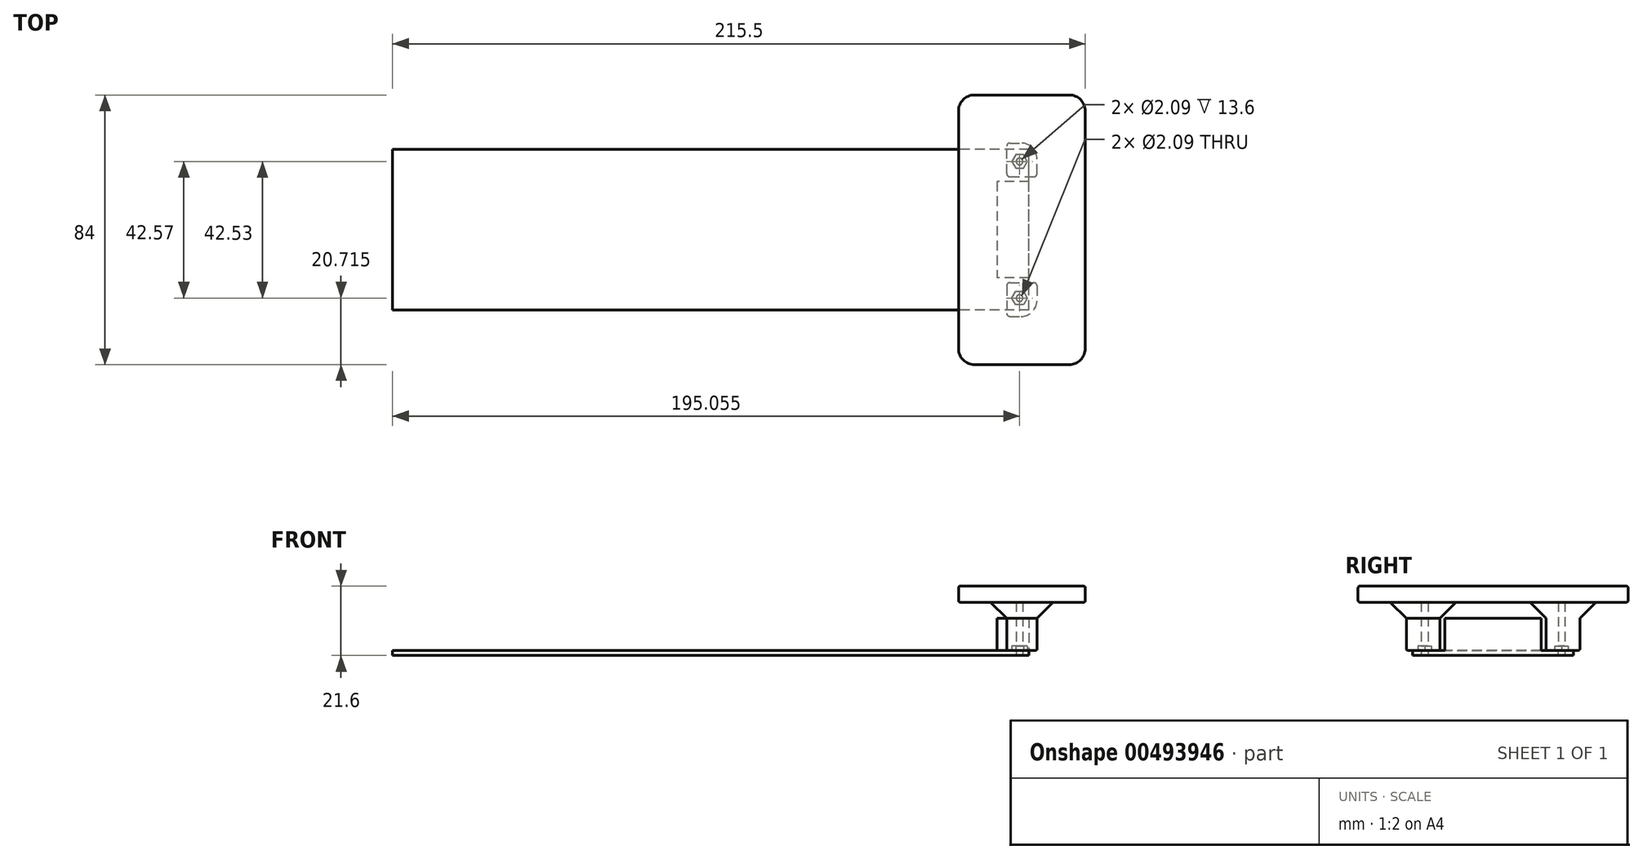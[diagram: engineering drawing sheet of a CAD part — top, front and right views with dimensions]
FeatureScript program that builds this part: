
annotation { "Feature Type Name" : "Feature", "Feature Type Description" : "" }
export const myFeature = defineFeature(function(context is Context, id is Id, definition is map)
    precondition{}
    {
        {
            var Q0;
            Q0=qCreatedBy(makeId("Top.planeOp"),FACE);
            var sketch = newSketch(context, id + "F0", { "sketchPlane" : qUnion([Q0])});
            skLineSegment(sketch, "E0.bottom", {"start": v(0, 0) * mm, "end": v(-198, 0) * mm});
            skLineSegment(sketch, "E0.top", {"start": v(0, 50) * mm, "end": v(-198, 50) * mm});
            skLineSegment(sketch, "E0.left", {"start": v(0, 0) * mm, "end": v(0, 50) * mm});
            skLineSegment(sketch, "E0.right", {"start": v(-198, 0) * mm, "end": v(-198, 50) * mm});
            skCircle(sketch, "E1", {"center": v(-2.95, 3.71) * mm, "radius": 1.04 * mm});
            skCircle(sketch, "E2", {"center": v(-2.95, 46.25) * mm, "radius": 1.04 * mm});
            skLineSegment(sketch, "E3", {"start": v(-2.95, 47.3) * mm, "end": v(-2.95, 50) * mm, "construction": true});
            skLineSegment(sketch, "E4", {"start": v(-1.9, 46.25) * mm, "end": v(0, 46.25) * mm, "construction": true});
            skLineSegment(sketch, "E5", {"start": v(0, 3.71) * mm, "end": v(-1.9, 3.71) * mm, "construction": true});
            skLineSegment(sketch, "E6", {"start": v(-2.95, 2.67) * mm, "end": v(-2.94, 0) * mm, "construction": true});
            skSolve(sketch);
        }
        {
            var Q0;
            Q0 = qSketchRegion(id + "F0", true);
            extrude(context, id + "F1", {"entities" : qUnion([Q0]), "depth" : 1.6 * mm});
        }
        {
            var Q0;
            Q0=makeQuery(id+"F1.opExtrude","CAP_FACE",FACE,{"disambiguationData":[OSD([sQuery(id+"F0.wireOp",EDGE,"E0.bottom"),sQuery(id+"F0.wireOp",EDGE,"E0.top"),sQuery(id+"F0.wireOp",EDGE,"E0.left"),sQuery(id+"F0.wireOp",EDGE,"E0.right"),sQuery(id+"F0.wireOp",EDGE,"E1"),sQuery(id+"F0.wireOp",EDGE,"E2")])],"isStart":false});
            var sketch = newSketch(context, id + "F2", { "sketchPlane" : qUnion([Q0])});
            skLineSegment(sketch, "E7.bottom", {"start": v(0, 40) * mm, "end": v(-10, 40) * mm});
            skLineSegment(sketch, "E7.top", {"start": v(0, 10) * mm, "end": v(-10, 10) * mm});
            skLineSegment(sketch, "E7.left", {"start": v(0, 40) * mm, "end": v(0, 10) * mm});
            skLineSegment(sketch, "E7.right", {"start": v(-10, 40) * mm, "end": v(-10, 10) * mm});
            skLineSegment(sketch, "E8", {"start": v(-10, 40) * mm, "end": v(-10, 50) * mm, "construction": true});
            skLineSegment(sketch, "E9", {"start": v(-10, 10) * mm, "end": v(-10, 0) * mm, "construction": true});
            skSolve(sketch);
        }
        {
            var Q0;
            Q0=makeQuery(id+"F2.imprint","IMPRINT",FACE,{"disambiguationData":[TD([[makeQuery(id+"F2.imprint","IMPRINT",EDGE,{"derivedFrom":sQuery(id+"F2.wireOp",EDGE,"E7.bottom")}),1.0]])]});
            extrude(context, id + "F3", {"entities" : qUnion([Q0]), "operationType" : NewBodyOperationType.ADD, "depth" : 10 * mm});
        }
        {
            var Q0;
            Q0=makeQuery(id+"F1.opExtrude","CAP_FACE",FACE,{"disambiguationData":[OSD([sQuery(id+"F0.wireOp",EDGE,"E0.bottom"),sQuery(id+"F0.wireOp",EDGE,"E0.top"),sQuery(id+"F0.wireOp",EDGE,"E0.left"),sQuery(id+"F0.wireOp",EDGE,"E0.right"),sQuery(id+"F0.wireOp",EDGE,"E1"),sQuery(id+"F0.wireOp",EDGE,"E2")])],"isStart":false});
            var sketch = newSketch(context, id + "F4", { "sketchPlane" : qUnion([Q0])});
            skCircle(sketch, "E10", {"center": v(-2.95, 3.71) * mm, "radius": 0.85 * mm});
            skLineSegment(sketch, "E11.bottom", {"start": v(-6.95, 8.5) * mm, "end": v(2.5, 8.5) * mm});
            skLineSegment(sketch, "E11.top", {"start": v(-6.94, -2) * mm, "end": v(2.5, -2) * mm});
            skLineSegment(sketch, "E11.left", {"start": v(-6.95, 8.5) * mm, "end": v(-6.95, -2) * mm});
            skLineSegment(sketch, "E11.right", {"start": v(2.5, 8.5) * mm, "end": v(2.5, -2) * mm});
            skLineSegment(sketch, "E12", {"start": v(-6.95, 3.71) * mm, "end": v(2.5, 3.71) * mm, "construction": true});
            skLineSegment(sketch, "E13", {"start": v(-2.95, -2) * mm, "end": v(-2.95, 8.5) * mm, "construction": true});
            skLineSegment(sketch, "E14.0", {"start": v(0, 0) * mm, "end": v(-198, 0) * mm, "construction": true});
            skLineSegment(sketch, "E14.1", {"start": v(0, 0) * mm, "end": v(0, 10) * mm, "construction": true});
            skSolve(sketch);
        }
        {
            var Q0;
            {var subQ2=sQuery(id+"F4.wireOp",EDGE,"E11.top");Q0=makeQuery(id+"F4.imprint","IMPRINT",FACE,{"disambiguationData":[TD([[makeQuery(id+"F4.imprint","IMPRINT",EDGE,{"derivedFrom":subQ2}),1.0]])]});}
            var Q1;
            {var subQ0=sQuery(id+"F0.wireOp",EDGE,"E1");Q1=makeQuery(id+"F4.imprint","IMPRINT",FACE,{"disambiguationData":[TD([[makeQuery(id+"F4.imprint","IMPRINT",EDGE,{"derivedFrom":makeQuery(id+"F1.opExtrude","CAP_EDGE",EDGE,{"disambiguationData":[OSD([subQ0])],"isStart":false})}),-1.0]])]});}
            extrude(context, id + "F5", {"entities" : qUnion([Q0, Q1]), "depth" : 15 * mm});
        }
        {
            var Q0;
            Q0=makeQuery(id+"F5.opExtrude","SWEPT_EDGE",EDGE,{"disambiguationData":[OSD([sQuery(id+"F4.wireOp",EDGE,"E11.top"),sQuery(id+"F4.wireOp",EDGE,"E11.right")])]});
            fillet(context, id + "F6", {"entities" : qUnion([Q0]), "radius" : 5 * mm, "tangentPropagation" : true, "allowEdgeOverflow" : false});
        }
        {
            var Q0;
            Q0=makeQuery(id+"F5.opExtrude","CAP_FACE",FACE,{"disambiguationData":[OSD([sQuery(id+"F0.wireOp",EDGE,"E1"),sQuery(id+"F4.wireOp",EDGE,"E11.bottom"),sQuery(id+"F4.wireOp",EDGE,"E11.top"),sQuery(id+"F4.wireOp",EDGE,"E11.left"),sQuery(id+"F4.wireOp",EDGE,"E11.right")])],"isStart":true});
            var sketch = newSketch(context, id + "F7", { "sketchPlane" : qUnion([Q0])});
            skCircle(sketch, "E15", {"center": v(-2.95, -3.71) * mm, "radius": 2.1 * mm, "construction": true});
            skLineSegment(sketch, "E16", {"start": v(-1.73, -1.61) * mm, "end": v(-4.16, -1.61) * mm});
            skLineSegment(sketch, "E17", {"start": v(-4.16, -1.61) * mm, "end": v(-5.37, -3.71) * mm});
            skLineSegment(sketch, "E18", {"start": v(-5.37, -3.71) * mm, "end": v(-4.16, -5.81) * mm});
            skLineSegment(sketch, "E19", {"start": v(-4.16, -5.81) * mm, "end": v(-1.73, -5.81) * mm});
            skLineSegment(sketch, "E20", {"start": v(-1.73, -5.81) * mm, "end": v(-0.52, -3.72) * mm});
            skLineSegment(sketch, "E21", {"start": v(-0.52, -3.71) * mm, "end": v(-1.73, -1.61) * mm});
            skSolve(sketch);
        }
        {
            var Q0;
            Q0 = qSketchRegion(id + "F7", true);
            extrude(context, id + "F8", {"entities" : qUnion([Q0]), "operationType" : NewBodyOperationType.REMOVE, "oppositeDirection" : true, "depth" : 1.4 * mm, "offsetDistance" : 25 * mm});
        }
        {
            var Q0;
            Q0=makeQuery(id+"F5.opExtrude","SWEPT_EDGE",EDGE,{"disambiguationData":[OSD([sQuery(id+"F4.wireOp",EDGE,"E11.top"),sQuery(id+"F4.wireOp",EDGE,"E11.left")])]});
            var Q1;
            Q1=makeQuery(id+"F5.opExtrude","SWEPT_EDGE",EDGE,{"disambiguationData":[OSD([sQuery(id+"F4.wireOp",EDGE,"E11.bottom"),sQuery(id+"F4.wireOp",EDGE,"E11.right")])]});
            var Q2;
            Q2=makeQuery(id+"F5.opExtrude","SWEPT_EDGE",EDGE,{"disambiguationData":[OSD([sQuery(id+"F4.wireOp",EDGE,"E11.bottom"),sQuery(id+"F4.wireOp",EDGE,"E11.left")])]});
            fillet(context, id + "F9", {"entities" : qUnion([Q0, Q1, Q2]), "radius" : 1 * mm, "tangentPropagation" : true, "allowEdgeOverflow" : false});
        }
        {
            var Q0;
            Q0=makeQuery(id+"F1.opExtrude","CAP_EDGE",EDGE,{"disambiguationData":[OSD([sQuery(id+"F0.wireOp",EDGE,"E0.left")])],"isStart":true});
            cPoint(context, id + "F10", {"entities" : qUnion([Q0]), "parameter" : 0.5});
        }
        {
            var Q0;
            Q0=makeQuery(id+"F3.opExtrude","CAP_EDGE",EDGE,{"disambiguationData":[OSD([sQuery(id+"F2.wireOp",EDGE,"E7.left")])],"isStart":false});
            cPoint(context, id + "F11", {"entities" : qUnion([Q0]), "parameter" : 0.5});
        }
        {
            var Q0;
            Q0=makeQuery(id+"F3.opExtrude","CAP_EDGE",EDGE,{"disambiguationData":[OSD([sQuery(id+"F2.wireOp",EDGE,"E7.right")])],"isStart":false});
            cPoint(context, id + "F12", {"entities" : qUnion([Q0]), "parameter" : 0.5});
        }
        {
            var Q0;
            Q0 = qCreatedBy(id + "F10" ,VERTEX);
            var Q1;
            Q1 = qCreatedBy(id + "F11" ,VERTEX);
            var Q2;
            Q2 = qCreatedBy(id + "F12" ,VERTEX);
            cPlane(context, id + "F13", {"entities" : qUnion([Q0, Q1, Q2]), "cplaneType" : CPlaneType.THREE_POINT, "offset" : 25 * mm, "width" : 150 * mm, "height" : 150 * mm});
        }
        {
            var Q0;
            Q0=makeQuery(id+"F5.opExtrude","SWEPT_BODY",BODY,{"disambiguationData":[OSD([sQuery(id+"F0.wireOp",EDGE,"E1"),sQuery(id+"F4.wireOp",EDGE,"E11.bottom"),sQuery(id+"F4.wireOp",EDGE,"E11.top"),sQuery(id+"F4.wireOp",EDGE,"E11.left"),sQuery(id+"F4.wireOp",EDGE,"E11.right")])]});
            var Q1;
            Q1=qCreatedBy(id+"F13.planeOp",FACE);
            mirror(context, id + "F14", {"entities" : qUnion([Q0]), "mirrorPlane" : qUnion([Q1])});
        }
        {
            var Q0;
            Q0=makeQuery(id+"F5.opExtrude","CAP_FACE",FACE,{"disambiguationData":[OSD([sQuery(id+"F0.wireOp",EDGE,"E1"),sQuery(id+"F4.wireOp",EDGE,"E11.bottom"),sQuery(id+"F4.wireOp",EDGE,"E11.top"),sQuery(id+"F4.wireOp",EDGE,"E11.left"),sQuery(id+"F4.wireOp",EDGE,"E11.right")])],"isStart":false});
            var sketch = newSketch(context, id + "F15", { "sketchPlane" : qUnion([Q0])});
            skLineSegment(sketch, "E22.bottom", {"start": v(-21.94, -17) * mm, "end": v(17.5, -17) * mm});
            skLineSegment(sketch, "E22.top", {"start": v(-21.95, 67) * mm, "end": v(17.5, 67) * mm});
            skLineSegment(sketch, "E22.left", {"start": v(-21.94, -17) * mm, "end": v(-21.95, 67) * mm});
            skLineSegment(sketch, "E22.right", {"start": v(17.5, -17) * mm, "end": v(17.5, 67) * mm});
            skLineSegment(sketch, "E23.2", {"start": v(17.5, 67) * mm, "end": v(17.5, -17) * mm});
            skPoint(sketch, "E24", {"position": v(17.5, 67) * mm});
            skPoint(sketch, "E25.0", {"position": v(0, 25) * mm});
            skPoint(sketch, "E26", {"position": v(17.5, 25) * mm});
            skSolve(sketch);
        }
        {
            var Q0;
            Q0=makeQuery(id+"F15.imprint","IMPRINT",FACE,{"disambiguationData":[TD([[makeQuery(id+"F15.imprint","IMPRINT",EDGE,{"derivedFrom":sQuery(id+"F15.wireOp",EDGE,"E22.top")}),-1.0]])]});
            var Q1;
            {var subQ4=sQuery(id+"F0.wireOp",EDGE,"E1");Q1=makeQuery(id+"F15.imprint","IMPRINT",FACE,{"disambiguationData":[TD([[makeQuery(id+"F15.imprint","IMPRINT",EDGE,{"derivedFrom":makeQuery(id+"F5.opExtrude","CAP_EDGE",EDGE,{"disambiguationData":[OSD([subQ4])],"isStart":false})}),-1.0]])]});}
            var Q2;
            Q2=makeQuery(id+"F15.imprint","IMPRINT",FACE,{"disambiguationData":[TD([[makeQuery(id+"F15.imprint","IMPRINT",EDGE,{"derivedFrom":makeQuery(id+"F5.opExtrude","CAP_EDGE",EDGE,{"disambiguationData":[OSD([sQuery(id+"F0.wireOp",EDGE,"E1")])],"isStart":false})}),1.0]])]});
            extrude(context, id + "F16", {"entities" : qUnion([Q0, Q1, Q2]), "operationType" : NewBodyOperationType.ADD, "depth" : 5 * mm});
        }
        {
            var Q0;
            {var subQ0=sQuery(id+"F4.wireOp",EDGE,"E11.right");var subQ1=sQuery(id+"F4.wireOp",EDGE,"E11.top");Q0=makeQuery(id+"F14.opPattern","COPY",EDGE,{"derivedFrom":makeQuery(id+"F6.opFillet","BLEND_EDGE",EDGE,{"blendedFrom":[makeQuery(id+"F5.opExtrude","SWEPT_EDGE",EDGE,{"disambiguationData":[OSD([subQ1,subQ0])]}),makeQuery(id+"F5.opExtrude","CAP_FACE",FACE,{"disambiguationData":[OSD([sQuery(id+"F0.wireOp",EDGE,"E1"),sQuery(id+"F4.wireOp",EDGE,"E11.bottom"),subQ1,sQuery(id+"F4.wireOp",EDGE,"E11.left"),subQ0])],"isStart":false})],"blendedInto":[makeQuery(id+"F5.opExtrude","CAP_FACE",FACE,{"disambiguationData":[OSD([sQuery(id+"F0.wireOp",EDGE,"E1"),sQuery(id+"F4.wireOp",EDGE,"E11.bottom"),subQ1,sQuery(id+"F4.wireOp",EDGE,"E11.left"),subQ0])],"isStart":false})]}),"instanceName":"1"});}
            var Q1;
            Q1=makeQuery(id+"F5.opExtrude","CAP_EDGE",EDGE,{"disambiguationData":[OSD([sQuery(id+"F4.wireOp",EDGE,"E11.right")])],"isStart":false});
            chamfer(context, id + "F17", {"entities" : qUnion([Q0, Q1]), "width" : 5 * mm, "tangentPropagation" : true});
        }
        {
            var Q0;
            Q0=makeQuery(id+"F16.opExtrude","SWEPT_EDGE",EDGE,{"disambiguationData":[OSD([sQuery(id+"F15.wireOp",EDGE,"E22.top"),sQuery(id+"F15.wireOp",EDGE,"E22.left")])]});
            var Q1;
            Q1=makeQuery(id+"F16.opExtrude","SWEPT_EDGE",EDGE,{"disambiguationData":[OSD([sQuery(id+"F15.wireOp",EDGE,"E22.top"),sQuery(id+"F15.wireOp",EDGE,"E23.2")])]});
            var Q2;
            Q2=makeQuery(id+"F16.opExtrude","SWEPT_EDGE",EDGE,{"disambiguationData":[OSD([sQuery(id+"F15.wireOp",EDGE,"E22.bottom"),sQuery(id+"F15.wireOp",EDGE,"E23.2")])]});
            var Q3;
            Q3=makeQuery(id+"F16.opExtrude","SWEPT_EDGE",EDGE,{"disambiguationData":[OSD([sQuery(id+"F15.wireOp",EDGE,"E22.left"),sQuery(id+"F15.wireOp",EDGE,"E22.bottom")])]});
            fillet(context, id + "F18", {"entities" : qUnion([Q0, Q1, Q2, Q3]), "radius" : 5 * mm, "tangentPropagation" : true, "allowEdgeOverflow" : false});
        }
        {
            var Q0;
            {var subQ4=sQuery(id+"F4.wireOp",EDGE,"E11.bottom");var subQ8=makeQuery(id+"F5.opExtrude","SWEPT_FACE",FACE,{"disambiguationData":[OSD([subQ4])]});var subQ12=sQuery(id+"F15.wireOp",EDGE,"E22.top");var subQ13=sQuery(id+"F15.wireOp",EDGE,"E22.left");var subQ14=sQuery(id+"F15.wireOp",EDGE,"E22.bottom");var subQ15=sQuery(id+"F15.wireOp",EDGE,"E23.2");Q0=makeQuery(id+"F16.boolean.opBoolean","SPLIT",FACE,{"disambiguationData":[TD([subQ8])],"derivedFrom":makeQuery(id+"F16.opExtrude","CAP_FACE",FACE,{"disambiguationData":[OSD([subQ12,subQ13,subQ14,subQ15])],"isStart":true})});}
            var Q1;
            Q1=makeQuery(id+"F16.opExtrude","CAP_FACE",FACE,{"disambiguationData":[OSD([sQuery(id+"F15.wireOp",EDGE,"E22.top"),sQuery(id+"F15.wireOp",EDGE,"E22.left"),sQuery(id+"F15.wireOp",EDGE,"E22.bottom"),sQuery(id+"F15.wireOp",EDGE,"E23.2")])],"isStart":false});
            var Q2;
            {var subQ0=sQuery(id+"F4.wireOp",EDGE,"E11.right");Q2=makeQuery(id+"F17.opChamfer","BLEND_EDGE",EDGE,{"blendedFrom":[makeQuery(id+"F14.opPattern","COPY",EDGE,{"derivedFrom":makeQuery(id+"F5.opExtrude","CAP_EDGE",EDGE,{"disambiguationData":[OSD([subQ0])],"isStart":false}),"instanceName":"1"}),makeQuery(id+"F14.opPattern","COPY",FACE,{"derivedFrom":makeQuery(id+"F5.opExtrude","SWEPT_FACE",FACE,{"disambiguationData":[OSD([subQ0])]}),"instanceName":"1"})],"blendedInto":[makeQuery(id+"F14.opPattern","COPY",FACE,{"derivedFrom":makeQuery(id+"F5.opExtrude","SWEPT_FACE",FACE,{"disambiguationData":[OSD([subQ0])]}),"instanceName":"1"})]});}
            var Q3;
            Q3=makeQuery(id+"F5.opExtrude","CAP_EDGE",EDGE,{"disambiguationData":[OSD([sQuery(id+"F4.wireOp",EDGE,"E11.top")])],"isStart":true});
            var Q4;
            Q4=makeQuery(id+"F14.opPattern","COPY",EDGE,{"derivedFrom":makeQuery(id+"F5.opExtrude","CAP_EDGE",EDGE,{"disambiguationData":[OSD([sQuery(id+"F4.wireOp",EDGE,"E11.bottom")])],"isStart":true}),"instanceName":"1"});
            fillet(context, id + "F19", {"entities" : qUnion([Q0, Q1, Q2, Q3, Q4]), "radius" : .5 * mm, "tangentPropagation" : true, "allowEdgeOverflow" : false});
        }
    });
